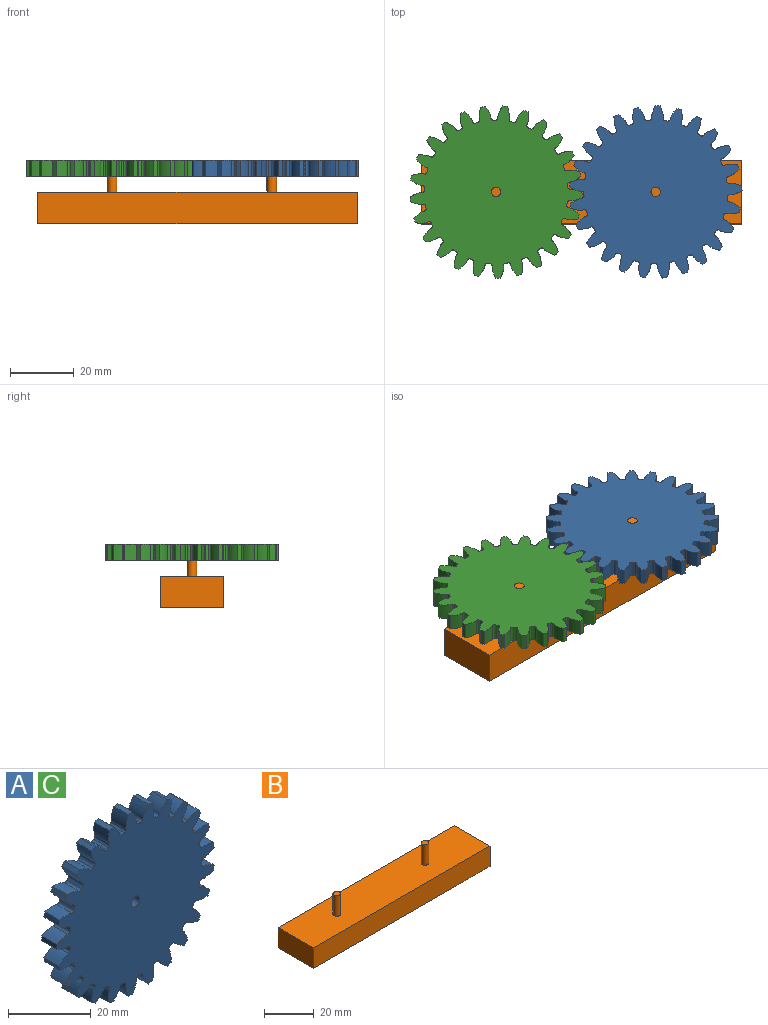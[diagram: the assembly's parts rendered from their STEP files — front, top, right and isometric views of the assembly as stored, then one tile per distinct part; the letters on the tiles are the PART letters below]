
ASSEMBLY  parts=3 mates=2
PART A: 153 faces, bbox 53.9x5.1x54 mm
  f0: extruded ~5.08x3.69mm, area 20.6mm2, adj f100,f101,f102,f103
  f1: cylinder r=22.5mm len=5.08mm, axis (0,1,0), area 3.9mm2, adj f101,f102,f103,f104
  f2: extruded ~5.08x3.69mm, area 20.6mm2, adj f3,f101,f102,f104
  f3: cylinder r=27mm len=5.08mm, axis (0,1,0), area 7.3mm2, adj f2,f4,f101,f102
  f4: extruded ~5.08x3.96mm, area 20.6mm2, adj f3,f101,f102,f105
  f5: cylinder r=22.5mm len=5.08mm, axis (0,1,0), area 3.9mm2, adj f101,f102,f105,f106
  f6: extruded ~5.08x3.18mm, area 20.6mm2, adj f7,f101,f102,f106
  f7: cylinder r=27mm len=5.08mm, axis (0,1,0), area 7.3mm2, adj f6,f8,f101,f102
  f8: extruded ~5.08x3.98mm, area 20.6mm2, adj f7,f101,f102,f107
  f9: cylinder r=22.5mm len=5.08mm, axis (0,1,0), area 3.9mm2, adj f101,f102,f107,f108
  f10: extruded ~5.08x3.14mm, area 20.6mm2, adj f11,f101,f102,f108
  f11: cylinder r=27mm len=5.08mm, axis (0,1,0), area 7.3mm2, adj f10,f12,f101,f102
  f12: extruded ~5.08x3.76mm, area 20.6mm2, adj f11,f101,f102,f109
  f13: cylinder r=22.5mm len=5.08mm, axis (0,1,0), area 3.9mm2, adj f101,f102,f109,f110
  f14: extruded ~5.08x3.66mm, area 20.6mm2, adj f15,f101,f102,f110
  f15: cylinder r=27mm len=5.08mm, axis (0,1,0), area 7.3mm2, adj f14,f16,f101,f102
  f16: extruded ~5.08x3.29mm, area 20.6mm2, adj f15,f101,f102,f111
  f17: cylinder r=22.5mm len=5.08mm, axis (0,1,0), area 3.9mm2, adj f101,f102,f111,f112
  f18: extruded ~5.08x3.95mm, area 20.6mm2, adj f19,f101,f102,f112
  f19: cylinder r=27mm len=5.08mm, axis (0,1,0), area 7.3mm2, adj f18,f20,f101,f102
  f20: extruded ~5.08x3.03mm, area 20.6mm2, adj f19,f101,f102,f113
  f21: cylinder r=22.5mm len=5.08mm, axis (0,1,0), area 3.9mm2, adj f101,f102,f113,f114
  f22: extruded ~5.08x3.99mm, area 20.6mm2, adj f23,f101,f102,f114
  f23: cylinder r=27mm len=5.08mm, axis (0,1,0), area 7.3mm2, adj f22,f24,f101,f102
  f24: extruded ~5.08x3.58mm, area 20.6mm2, adj f23,f101,f102,f115
  f25: cylinder r=22.5mm len=5.08mm, axis (0,1,0), area 3.9mm2, adj f101,f102,f115,f116
  f26: extruded ~5.08x3.78mm, area 20.6mm2, adj f27,f101,f102,f116
  f27: cylinder r=27mm len=5.08mm, axis (0,1,0), area 7.3mm2, adj f26,f28,f101,f102
  f28: extruded ~5.08x3.91mm, area 20.6mm2, adj f27,f101,f102,f117
  f29: cylinder r=22.5mm len=5.08mm, axis (0,1,0), area 3.9mm2, adj f101,f102,f117,f118
  f30: extruded ~5.08x3.33mm, area 20.6mm2, adj f31,f101,f102,f118
  f31: cylinder r=27mm len=5.08mm, axis (0,1,0), area 7.3mm2, adj f30,f32,f101,f102
  f32: extruded ~5.08x4mm, area 20.6mm2, adj f31,f101,f102,f119
  f33: cylinder r=22.5mm len=5.08mm, axis (0,1,0), area 3.9mm2, adj f101,f102,f119,f120
  f34: extruded ~5.08x2.98mm, area 20.6mm2, adj f35,f101,f102,f120
  f35: cylinder r=27mm len=5.08mm, axis (0,1,0), area 7.3mm2, adj f34,f36,f101,f102
  f36: extruded ~5.08x3.84mm, area 20.6mm2, adj f35,f101,f102,f121
  f37: cylinder r=22.5mm len=5.08mm, axis (0,1,0), area 3.9mm2, adj f101,f102,f121,f122
  f38: extruded ~5.08x3.55mm, area 20.6mm2, adj f39,f101,f102,f122
  f39: cylinder r=27mm len=5.08mm, axis (0,1,0), area 7.3mm2, adj f38,f40,f101,f102
  f40: extruded ~5.08x3.43mm, area 20.6mm2, adj f39,f101,f102,f123
  f41: cylinder r=22.5mm len=5.08mm, axis (0,1,0), area 3.9mm2, adj f101,f102,f123,f124
  f42: extruded ~5.08x3.9mm, area 20.6mm2, adj f43,f101,f102,f124
  f43: cylinder r=27mm len=5.08mm, axis (0,1,0), area 7.3mm2, adj f42,f44,f101,f102
  f44: extruded ~5.08x2.85mm, area 20.6mm2, adj f43,f101,f102,f125
  f45: cylinder r=22.5mm len=5.08mm, axis (0,1,0), area 3.9mm2, adj f101,f102,f125,f126
  f46: extruded ~5.08x4mm, area 20.6mm2, adj f47,f101,f102,f126
  f47: cylinder r=27mm len=5.08mm, axis (0,1,0), area 7.3mm2, adj f46,f48,f101,f102
  f48: extruded ~5.08x3.46mm, area 20.6mm2, adj f47,f101,f102,f127
  f49: cylinder r=22.5mm len=5.08mm, axis (0,1,0), area 3.9mm2, adj f101,f102,f127,f128
  f50: extruded ~5.08x3.85mm, area 20.6mm2, adj f51,f101,f102,f128
  f51: cylinder r=27mm len=5.08mm, axis (0,1,0), area 7.3mm2, adj f50,f52,f101,f102
  f52: extruded ~5.08x3.85mm, area 20.6mm2, adj f51,f101,f102,f129
  f53: cylinder r=22.5mm len=5.08mm, axis (0,1,0), area 3.9mm2, adj f101,f102,f129,f130
  f54: extruded ~5.08x3.46mm, area 20.6mm2, adj f55,f101,f102,f130
  f55: cylinder r=27mm len=5.08mm, axis (0,1,0), area 7.3mm2, adj f54,f56,f101,f102
  f56: extruded ~5.08x4mm, area 20.6mm2, adj f55,f101,f102,f131
  f57: cylinder r=22.5mm len=5.08mm, axis (0,1,0), area 3.9mm2, adj f101,f102,f131,f132
  f58: extruded ~5.08x2.85mm, area 20.6mm2, adj f59,f101,f102,f132
  f59: cylinder r=27mm len=5.08mm, axis (0,1,0), area 7.3mm2, adj f58,f60,f101,f102
  f60: extruded ~5.08x3.9mm, area 20.6mm2, adj f59,f101,f102,f133
  f61: cylinder r=22.5mm len=5.08mm, axis (0,1,0), area 3.9mm2, adj f101,f102,f133,f134
  f62: extruded ~5.08x3.43mm, area 20.6mm2, adj f63,f101,f102,f134
  f63: cylinder r=27mm len=5.08mm, axis (0,1,0), area 7.3mm2, adj f62,f64,f101,f102
  f64: extruded ~5.08x3.55mm, area 20.6mm2, adj f63,f101,f102,f135
  f65: cylinder r=22.5mm len=5.08mm, axis (0,1,0), area 3.9mm2, adj f101,f102,f135,f136
  f66: extruded ~5.08x3.84mm, area 20.6mm2, adj f67,f101,f102,f136
  f67: cylinder r=27mm len=5.08mm, axis (0,1,0), area 7.3mm2, adj f66,f68,f101,f102
  f68: extruded ~5.08x2.98mm, area 20.6mm2, adj f67,f101,f102,f137
  f69: cylinder r=22.5mm len=5.08mm, axis (0,1,0), area 3.9mm2, adj f101,f102,f137,f138
  f70: extruded ~5.08x4mm, area 20.6mm2, adj f71,f101,f102,f138
  f71: cylinder r=27mm len=5.08mm, axis (0,1,0), area 7.3mm2, adj f70,f72,f101,f102
  f72: extruded ~5.08x3.33mm, area 20.6mm2, adj f71,f101,f102,f139
  f73: cylinder r=22.5mm len=5.08mm, axis (0,1,0), area 3.9mm2, adj f101,f102,f139,f140
  f74: extruded ~5.08x3.91mm, area 20.6mm2, adj f75,f101,f102,f140
  f75: cylinder r=27mm len=5.08mm, axis (0,1,0), area 7.3mm2, adj f74,f76,f101,f102
  f76: extruded ~5.08x3.78mm, area 20.6mm2, adj f75,f101,f102,f141
  f77: cylinder r=22.5mm len=5.08mm, axis (0,1,0), area 3.9mm2, adj f101,f102,f141,f142
  f78: extruded ~5.08x3.58mm, area 20.6mm2, adj f79,f101,f102,f142
  f79: cylinder r=27mm len=5.08mm, axis (0,1,0), area 7.3mm2, adj f78,f80,f101,f102
  f80: extruded ~5.08x3.99mm, area 20.6mm2, adj f79,f101,f102,f143
  f81: cylinder r=22.5mm len=5.08mm, axis (0,1,0), area 3.9mm2, adj f101,f102,f143,f144
  f82: extruded ~5.08x3.03mm, area 20.6mm2, adj f83,f101,f102,f144
  f83: cylinder r=27mm len=5.08mm, axis (0,1,0), area 7.3mm2, adj f82,f84,f101,f102
  f84: extruded ~5.08x3.95mm, area 20.6mm2, adj f83,f101,f102,f145
  f85: cylinder r=22.5mm len=5.08mm, axis (0,1,0), area 3.9mm2, adj f101,f102,f145,f146
  f86: extruded ~5.08x3.29mm, area 20.6mm2, adj f87,f101,f102,f146
  f87: cylinder r=27mm len=5.08mm, axis (0,1,0), area 7.3mm2, adj f86,f88,f101,f102
  f88: extruded ~5.08x3.66mm, area 20.6mm2, adj f87,f101,f102,f147
  f89: cylinder r=22.5mm len=5.08mm, axis (0,1,0), area 3.9mm2, adj f101,f102,f147,f148
  f90: extruded ~5.08x3.76mm, area 20.6mm2, adj f91,f101,f102,f148
  f91: cylinder r=27mm len=5.08mm, axis (0,1,0), area 7.3mm2, adj f90,f92,f101,f102
  f92: extruded ~5.08x3.14mm, area 20.6mm2, adj f91,f101,f102,f149
  f93: cylinder r=22.5mm len=5.08mm, axis (0,1,0), area 3.9mm2, adj f101,f102,f149,f150
  f94: extruded ~5.08x3.98mm, area 20.6mm2, adj f95,f101,f102,f150
  f95: cylinder r=27mm len=5.08mm, axis (0,1,0), area 7.3mm2, adj f94,f96,f101,f102
  f96: extruded ~5.08x3.18mm, area 20.6mm2, adj f95,f101,f102,f151
  f97: cylinder r=22.5mm len=5.08mm, axis (0,1,0), area 3.9mm2, adj f101,f102,f151,f152
  f98: extruded ~5.08x3.96mm, area 20.6mm2, adj f100,f101,f102,f152
  f99: cylinder r=1.5mm len=5.08mm, axis (0,1,0), area 47.9mm2, adj f101,f102
  f100: cylinder r=27mm len=5.08mm, axis (0,1,0), area 7.3mm2, adj f0,f98,f101,f102
  f101: plane 53.98x53.87mm, normal (0,-1,0), area 1926.9mm2, adj f0,f1,f2,f3,f4,f5,f6,f7
  f102: plane 53.98x53.87mm, normal (0,1,0), area 1926.9mm2, adj f0,f1,f2,f3,f4,f5,f6,f7
  f103: cylinder r=0.72mm len=5.08mm, axis (0,1,0), area 5.6mm2, adj f0,f1,f101,f102
  f104: cylinder r=0.72mm len=5.08mm, axis (0,1,0), area 5.6mm2, adj f1,f2,f101,f102
  f105: cylinder r=0.72mm len=5.08mm, axis (0,1,0), area 5.6mm2, adj f4,f5,f101,f102
  f106: cylinder r=0.72mm len=5.08mm, axis (0,1,0), area 5.6mm2, adj f5,f6,f101,f102
  f107: cylinder r=0.72mm len=5.08mm, axis (0,1,0), area 5.6mm2, adj f8,f9,f101,f102
  f108: cylinder r=0.72mm len=5.08mm, axis (0,1,0), area 5.6mm2, adj f9,f10,f101,f102
  f109: cylinder r=0.72mm len=5.08mm, axis (0,1,0), area 5.6mm2, adj f12,f13,f101,f102
  f110: cylinder r=0.72mm len=5.08mm, axis (0,1,0), area 5.6mm2, adj f13,f14,f101,f102
  f111: cylinder r=0.72mm len=5.08mm, axis (0,1,0), area 5.6mm2, adj f16,f17,f101,f102
  f112: cylinder r=0.72mm len=5.08mm, axis (0,1,0), area 5.6mm2, adj f17,f18,f101,f102
  f113: cylinder r=0.72mm len=5.08mm, axis (0,1,0), area 5.6mm2, adj f20,f21,f101,f102
  f114: cylinder r=0.72mm len=5.08mm, axis (0,1,0), area 5.6mm2, adj f21,f22,f101,f102
  f115: cylinder r=0.72mm len=5.08mm, axis (0,1,0), area 5.6mm2, adj f24,f25,f101,f102
  f116: cylinder r=0.72mm len=5.08mm, axis (0,1,0), area 5.6mm2, adj f25,f26,f101,f102
  f117: cylinder r=0.72mm len=5.08mm, axis (0,1,0), area 5.6mm2, adj f28,f29,f101,f102
  f118: cylinder r=0.72mm len=5.08mm, axis (0,1,0), area 5.6mm2, adj f29,f30,f101,f102
  f119: cylinder r=0.72mm len=5.08mm, axis (0,1,0), area 5.6mm2, adj f32,f33,f101,f102
  f120: cylinder r=0.72mm len=5.08mm, axis (0,1,0), area 5.6mm2, adj f33,f34,f101,f102
  f121: cylinder r=0.72mm len=5.08mm, axis (0,1,0), area 5.6mm2, adj f36,f37,f101,f102
  f122: cylinder r=0.72mm len=5.08mm, axis (0,1,0), area 5.6mm2, adj f37,f38,f101,f102
  f123: cylinder r=0.72mm len=5.08mm, axis (0,1,0), area 5.6mm2, adj f40,f41,f101,f102
  f124: cylinder r=0.72mm len=5.08mm, axis (0,1,0), area 5.6mm2, adj f41,f42,f101,f102
  f125: cylinder r=0.72mm len=5.08mm, axis (0,1,0), area 5.6mm2, adj f44,f45,f101,f102
  f126: cylinder r=0.72mm len=5.08mm, axis (0,1,0), area 5.6mm2, adj f45,f46,f101,f102
  f127: cylinder r=0.72mm len=5.08mm, axis (0,1,0), area 5.6mm2, adj f48,f49,f101,f102
  f128: cylinder r=0.72mm len=5.08mm, axis (0,1,0), area 5.6mm2, adj f49,f50,f101,f102
  f129: cylinder r=0.72mm len=5.08mm, axis (0,1,0), area 5.6mm2, adj f52,f53,f101,f102
  f130: cylinder r=0.72mm len=5.08mm, axis (0,1,0), area 5.6mm2, adj f53,f54,f101,f102
  f131: cylinder r=0.72mm len=5.08mm, axis (0,1,0), area 5.6mm2, adj f56,f57,f101,f102
  f132: cylinder r=0.72mm len=5.08mm, axis (0,1,0), area 5.6mm2, adj f57,f58,f101,f102
  f133: cylinder r=0.72mm len=5.08mm, axis (0,1,0), area 5.6mm2, adj f60,f61,f101,f102
  f134: cylinder r=0.72mm len=5.08mm, axis (0,1,0), area 5.6mm2, adj f61,f62,f101,f102
  f135: cylinder r=0.72mm len=5.08mm, axis (0,1,0), area 5.6mm2, adj f64,f65,f101,f102
  f136: cylinder r=0.72mm len=5.08mm, axis (0,1,0), area 5.6mm2, adj f65,f66,f101,f102
  f137: cylinder r=0.72mm len=5.08mm, axis (0,1,0), area 5.6mm2, adj f68,f69,f101,f102
  f138: cylinder r=0.72mm len=5.08mm, axis (0,1,0), area 5.6mm2, adj f69,f70,f101,f102
  f139: cylinder r=0.72mm len=5.08mm, axis (0,1,0), area 5.6mm2, adj f72,f73,f101,f102
  f140: cylinder r=0.72mm len=5.08mm, axis (0,1,0), area 5.6mm2, adj f73,f74,f101,f102
  f141: cylinder r=0.72mm len=5.08mm, axis (0,1,0), area 5.6mm2, adj f76,f77,f101,f102
  f142: cylinder r=0.72mm len=5.08mm, axis (0,1,0), area 5.6mm2, adj f77,f78,f101,f102
  f143: cylinder r=0.72mm len=5.08mm, axis (0,1,0), area 5.6mm2, adj f80,f81,f101,f102
  f144: cylinder r=0.72mm len=5.08mm, axis (0,1,0), area 5.6mm2, adj f81,f82,f101,f102
  f145: cylinder r=0.72mm len=5.08mm, axis (0,1,0), area 5.6mm2, adj f84,f85,f101,f102
  f146: cylinder r=0.72mm len=5.08mm, axis (0,1,0), area 5.6mm2, adj f85,f86,f101,f102
  f147: cylinder r=0.72mm len=5.08mm, axis (0,1,0), area 5.6mm2, adj f88,f89,f101,f102
  f148: cylinder r=0.72mm len=5.08mm, axis (0,1,0), area 5.6mm2, adj f89,f90,f101,f102
  f149: cylinder r=0.72mm len=5.08mm, axis (0,1,0), area 5.6mm2, adj f92,f93,f101,f102
  f150: cylinder r=0.72mm len=5.08mm, axis (0,1,0), area 5.6mm2, adj f93,f94,f101,f102
  f151: cylinder r=0.72mm len=5.08mm, axis (0,1,0), area 5.6mm2, adj f96,f97,f101,f102
  f152: cylinder r=0.72mm len=5.08mm, axis (0,1,0), area 5.6mm2, adj f97,f98,f101,f102
PART B: 10 faces, bbox 100x20x20 mm
  f0: plane 20x10mm, normal (1,0,0), area 200mm2, adj f1,f3,f4,f5
  f1: plane 100x10mm, normal (0,1,0), area 1000mm2, adj f0,f2,f4,f5
  f2: plane 20x10mm, normal (-1,0,0), area 200mm2, adj f1,f3,f4,f5
  f3: plane 100x10mm, normal (0,-1,0), area 1000mm2, adj f0,f2,f4,f5
  f4: plane 100x20mm, normal (0,0,1), area 1985.9mm2, adj f0,f1,f2,f3,f6,f8
  f5: plane 100x20mm, normal (0,0,-1), area 2000mm2, adj f0,f1,f2,f3
  f6: cylinder r=1.5mm len=10mm, axis (0,0,-1), area 94.2mm2, adj f4,f7
  f7: plane 3x3mm, normal (0,0,1), area 7.1mm2, adj f6
  f8: cylinder r=1.5mm len=10mm, axis (0,0,-1), area 94.2mm2, adj f4,f9
  f9: plane 3x3mm, normal (0,0,1), area 7.1mm2, adj f8
PART C: same geometry as A
PLACE A rot(axis=(-0.38,0.65,-0.65),138.7deg) t=(-41.67,-36.84,-6.79)mm
PLACE B t=(-64.92,-36.84,-21.71)mm fixed
PLACE C rot(axis=(-0.38,-0.65,0.65),138.7deg) t=(-91.67,-36.84,-6.79)mm
MATE revolute C.f3 <-> B.f6  axis (0,0,1) through (-91.67,-36.84,-1.71)mm
MATE revolute A.f3 <-> B.f8  axis (0,0,1) through (-41.67,-36.84,-1.71)mm
